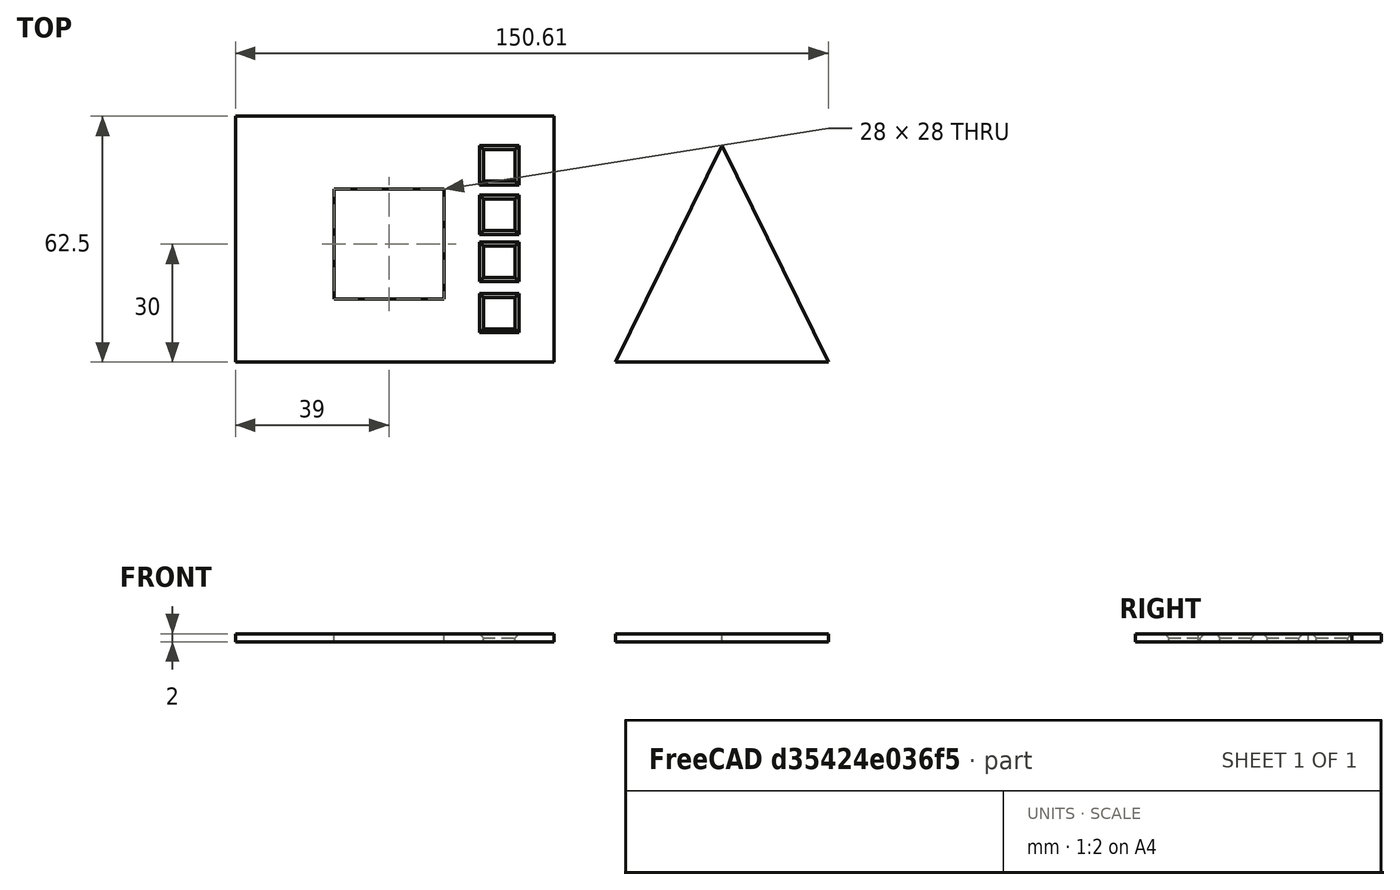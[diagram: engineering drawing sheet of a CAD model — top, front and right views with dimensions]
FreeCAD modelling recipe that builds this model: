
FCSTD DOCUMENT  (FreeCAD 0.17R13541 (Git))
Label: box
License: All rights reserved
LicenseURL: http://en.wikipedia.org/wiki/All_rights_reserved
objects: Part::Feature×7, Part::Extrusion×7, Part::MultiFuse×1, Part::Cut×1, Part::Chamfer×1
note: 17 computed .brp shape members not serialized (recipe doc carries the construction recipe); baked Part::Feature solids carry a one-line shape summary decoded from their .brp

FEATURE [Part::Feature] Wire
  shape: bbox 81 x 62.5 x 2e-07 mm, 0 faces, 0 solids (baked)
FEATURE [Part::Feature] Wire001
  shape: bbox 28 x 28 x 2e-07 mm, 0 faces, 0 solids (baked)
FEATURE [Part::Feature] Wire002 .. Wire005  x4 (patterned run collapsed; names and placements below)
  shape: bbox 8 x 8 x 2e-07 mm, 0 faces, 0 solids (baked)
FEATURE [Part::Feature] Wire006
  shape: bbox 54 x 55 x 2e-07 mm, 0 faces, 0 solids (baked)
FEATURE [Part::Extrusion] Extrude
  Base = -> Wire
  Dir = (0,0,1)
  DirMode = 0
  FaceMakerClass = Part::FaceMakerBullseye
  LengthFwd = 2
  LengthRev = 0
  Solid = true
  Symmetric = false
FEATURE [Part::Extrusion] Extrude001
  Base = -> Wire001
  Dir = (0,0,1)
  DirMode = 0
  FaceMakerClass = Part::FaceMakerBullseye
  LengthFwd = 2
  LengthRev = 0
  Solid = true
  Symmetric = false
FEATURE [Part::Extrusion] Extrude002
  Base = -> Wire002
  Dir = (0,0,1)
  DirMode = 0
  FaceMakerClass = Part::FaceMakerBullseye
  LengthFwd = 2
  LengthRev = 0
  Solid = true
  Symmetric = false
FEATURE [Part::Extrusion] Extrude003
  Base = -> Wire003
  Dir = (0,0,1)
  DirMode = 0
  FaceMakerClass = Part::FaceMakerBullseye
  LengthFwd = 2
  LengthRev = 0
  Solid = true
  Symmetric = false
FEATURE [Part::Extrusion] Extrude004
  Base = -> Wire004
  Dir = (0,0,1)
  DirMode = 0
  FaceMakerClass = Part::FaceMakerBullseye
  LengthFwd = 2
  LengthRev = 0
  Solid = true
  Symmetric = false
FEATURE [Part::Extrusion] Extrude005
  Base = -> Wire005
  Dir = (0,0,1)
  DirMode = 0
  FaceMakerClass = Part::FaceMakerBullseye
  LengthFwd = 2
  LengthRev = 0
  Solid = true
  Symmetric = false
FEATURE [Part::Extrusion] Extrude006
  Base = -> Wire006
  Dir = (0,0,1)
  DirMode = 0
  FaceMakerClass = Part::FaceMakerBullseye
  LengthFwd = 2
  LengthRev = 0
  Solid = true
  Symmetric = false
FEATURE [Part::MultiFuse] Fusion
  Shapes = -> [Extrude001,Extrude002,Extrude003,Extrude004,Extrude005]
FEATURE [Part::Cut] Cut
  Base = -> Extrude
  Tool = -> Fusion
FEATURE [Part::Chamfer] Chamfer
  Base = -> Cut
  Edges = 16 edges r=1: [Edge33,Edge34,Edge35,Edge36,Edge37,Edge38,Edge39,Edge40,Edge41,Edge42,Edge43,Edge44,Edge45,Edge46,Edge47,Edge48]
